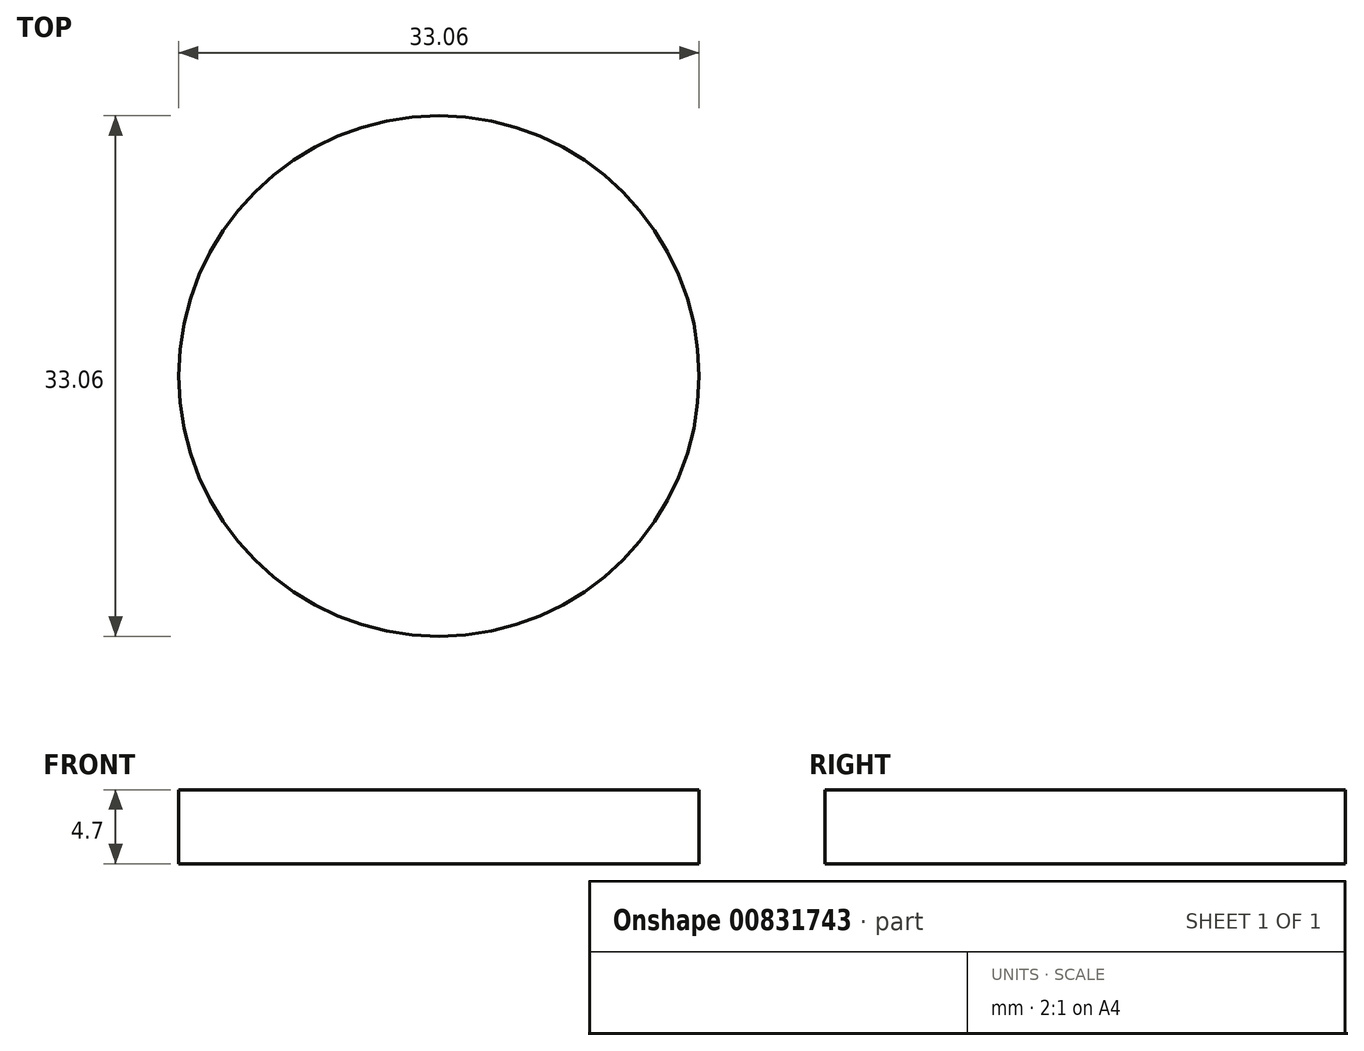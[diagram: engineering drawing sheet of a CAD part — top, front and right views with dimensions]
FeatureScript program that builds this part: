
annotation { "Feature Type Name" : "Feature", "Feature Type Description" : "" }
export const myFeature = defineFeature(function(context is Context, id is Id, definition is map)
    precondition{}
    {
        {
            var Q0;
            Q0=qCreatedBy(makeId("Top.planeOp"),FACE);
            var sketch = newSketch(context, id + "F0", { "sketchPlane" : qUnion([Q0])});
            skCircle(sketch, "E0", {"center": v(0.15, -0.45) * mm, "radius": 16.53 * mm});
            skSolve(sketch);
        }
        {
            var Q0;
            Q0=makeQuery(id+"F0.imprint","IMPRINT",FACE,{"disambiguationData":[TD([[makeQuery(id+"F0.imprint","IMPRINT",EDGE,{"derivedFrom":sQuery(id+"F0.wireOp",EDGE,"E0")}),1.0]])]});
            extrude(context, id + "F1", {"entities" : qUnion([Q0]), "depth" : 4.7 * mm, "offsetDistance" : 25 * mm});
        }
    });
